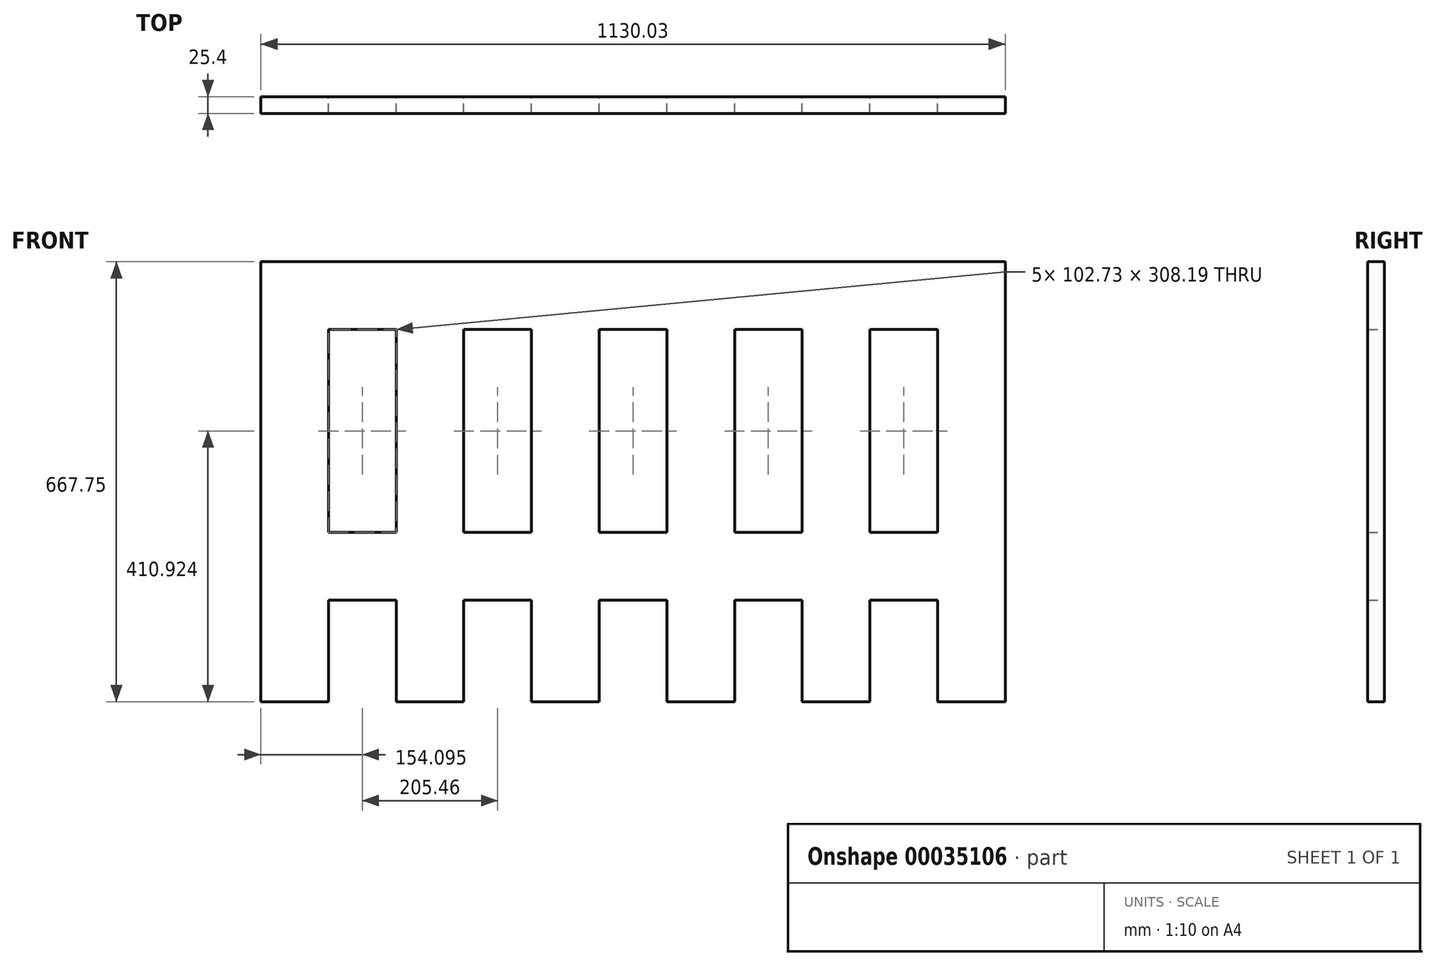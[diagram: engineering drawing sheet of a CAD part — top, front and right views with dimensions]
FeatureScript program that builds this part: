
annotation { "Feature Type Name" : "Feature", "Feature Type Description" : "" }
export const myFeature = defineFeature(function(context is Context, id is Id, definition is map)
    precondition{}
    {
        {
            var Q0;
            Q0=qCreatedBy(makeId("Front.planeOp"),FACE);
            var sketch = newSketch(context, id + "F0", { "sketchPlane" : qUnion([Q0])});
            skLineSegment(sketch, "E0", {"start": v(308.5, 268.75) * mm, "end": v(308.5, -399) * mm});
            skLineSegment(sketch, "E1", {"start": v(308.5, -399) * mm, "end": v(205.76, -399) * mm});
            skLineSegment(sketch, "E2", {"start": v(-821.54, -399) * mm, "end": v(-821.54, 268.75) * mm});
            skLineSegment(sketch, "E3", {"start": v(-821.54, 268.75) * mm, "end": v(308.5, 268.75) * mm});
            skLineSegment(sketch, "E4", {"start": v(-821.54, -244.9) * mm, "end": v(308.5, -244.9) * mm});
            skLineSegment(sketch, "E5", {"start": v(-821.54, -142.17) * mm, "end": v(308.5, -142.17) * mm});
            skLineSegment(sketch, "E6", {"start": v(-821.54, 166.02) * mm, "end": v(308.5, 166.02) * mm});
            skLineSegment(sketch, "E7", {"start": v(-718.81, 268.75) * mm, "end": v(-718.81, -399) * mm});
            skLineSegment(sketch, "E8", {"start": v(-616.08, 268.75) * mm, "end": v(-616.08, -399) * mm});
            skLineSegment(sketch, "E9", {"start": v(-513.35, 268.75) * mm, "end": v(-513.35, -399) * mm});
            skLineSegment(sketch, "E10", {"start": v(-410.62, 268.75) * mm, "end": v(-410.62, -399) * mm});
            skLineSegment(sketch, "E11", {"start": v(-307.89, 268.75) * mm, "end": v(-307.89, -399) * mm});
            skLineSegment(sketch, "E12", {"start": v(-205.16, 268.75) * mm, "end": v(-205.16, -399) * mm});
            skLineSegment(sketch, "E13", {"start": v(-102.43, 268.75) * mm, "end": v(-102.43, -399) * mm});
            skLineSegment(sketch, "E14", {"start": v(0.3, 268.75) * mm, "end": v(0.3, -399) * mm});
            skLineSegment(sketch, "E15", {"start": v(103.03, 268.75) * mm, "end": v(103.03, -399) * mm});
            skLineSegment(sketch, "E16", {"start": v(205.76, 268.75) * mm, "end": v(205.76, -399) * mm});
            skLineSegment(sketch, "E17.trimOffspring", {"start": v(-718.81, -399) * mm, "end": v(-821.54, -399) * mm});
            skLineSegment(sketch, "E18.trimOffspring", {"start": v(-513.35, -399) * mm, "end": v(-616.08, -399) * mm});
            skLineSegment(sketch, "E19.trimOffspring", {"start": v(-307.89, -399) * mm, "end": v(-410.62, -399) * mm});
            skLineSegment(sketch, "E20.trimOffspring", {"start": v(-102.43, -399) * mm, "end": v(-205.16, -399) * mm});
            skLineSegment(sketch, "E21.trimOffspring", {"start": v(103.03, -399) * mm, "end": v(0.3, -399) * mm});
            skLineSegment(sketch, "E22", {"start": v(-821.54, 268.75) * mm, "end": v(-821.54, 344.95) * mm});
            skLineSegment(sketch, "E23", {"start": v(308.5, 345.8) * mm, "end": v(308.5, 268.75) * mm});
            skLineSegment(sketch, "E24", {"start": v(-718.81, 268.75) * mm, "end": v(-718.87, 345.03) * mm});
            skLineSegment(sketch, "E25", {"start": v(-821.54, 344.95) * mm, "end": v(-770.18, 422.84) * mm});
            skLineSegment(sketch, "E26", {"start": v(-616.08, 268.75) * mm, "end": v(-616.14, 345.1) * mm});
            skLineSegment(sketch, "E27", {"start": v(-616.14, 345.1) * mm, "end": v(-564.72, 422.84) * mm});
            skLineSegment(sketch, "E28", {"start": v(-410.62, 268.75) * mm, "end": v(-410.68, 345.26) * mm});
            skLineSegment(sketch, "E29", {"start": v(-410.68, 345.26) * mm, "end": v(-359.25, 422.84) * mm});
            skLineSegment(sketch, "E30", {"start": v(-205.16, 268.75) * mm, "end": v(-205.16, 345.41) * mm});
            skLineSegment(sketch, "E31", {"start": v(-205.16, 345.41) * mm, "end": v(-153.8, 422.84) * mm});
            skLineSegment(sketch, "E32", {"start": v(0.3, 268.75) * mm, "end": v(0.3, 345.57) * mm});
            skLineSegment(sketch, "E33", {"start": v(0.3, 345.57) * mm, "end": v(51.67, 422.84) * mm});
            skLineSegment(sketch, "E34", {"start": v(205.76, 268.75) * mm, "end": v(205.76, 345.72) * mm});
            skLineSegment(sketch, "E35", {"start": v(205.76, 345.72) * mm, "end": v(257.13, 422.84) * mm});
            skLineSegment(sketch, "E36", {"start": v(-770.18, 422.84) * mm, "end": v(-718.87, 345.03) * mm});
            skLineSegment(sketch, "E37", {"start": v(-513.35, 268.75) * mm, "end": v(-513.35, 345.18) * mm});
            skLineSegment(sketch, "E38", {"start": v(-513.35, 345.18) * mm, "end": v(-564.72, 422.84) * mm});
            skLineSegment(sketch, "E39", {"start": v(-307.89, 268.75) * mm, "end": v(-307.89, 345.33) * mm});
            skLineSegment(sketch, "E40", {"start": v(-307.89, 345.33) * mm, "end": v(-359.25, 422.84) * mm});
            skLineSegment(sketch, "E41", {"start": v(-102.43, 268.75) * mm, "end": v(-102.43, 345.49) * mm});
            skLineSegment(sketch, "E42", {"start": v(-102.43, 345.49) * mm, "end": v(-153.8, 422.84) * mm});
            skLineSegment(sketch, "E43", {"start": v(103.03, 268.75) * mm, "end": v(103.03, 345.64) * mm});
            skLineSegment(sketch, "E44", {"start": v(103.03, 345.64) * mm, "end": v(51.67, 422.84) * mm});
            skLineSegment(sketch, "E45", {"start": v(257.13, 422.84) * mm, "end": v(308.5, 345.8) * mm});
            skSolve(sketch);
        }
        {
            var Q0;
            {var subQ1=sQuery(id+"F0.wireOp",EDGE,"c169b1e0-b60f-4d37-8ace-ff5277b2fe1d");Q0=makeQuery(id+"F0.imprint","IMPRINT",FACE,{"disambiguationData":[TD([[makeQuery(id+"F0.imprint","IMPRINT",EDGE,{"derivedFrom":subQ1}),-1.0]])]});}
            var Q1;
            {var subQ1=sQuery(id+"F0.wireOp",EDGE,"E6");var subQ5=sQuery(id+"F0.wireOp",EDGE,"E2");var subQ6=makeQuery(id+"F0.imprint","INTERSECT",VERTEX,{"derivedFrom":[subQ5,subQ1]});Q1=makeQuery(id+"F0.imprint","IMPRINT",FACE,{"disambiguationData":[TD([[makeQuery(id+"F0.imprint","IMPRINT",EDGE,{"disambiguationData":[TD([[subQ6,-1.0]])],"derivedFrom":subQ1}),1.0]])]});}
            var Q2;
            {var subQ3=sQuery(id+"F0.wireOp",EDGE,"E5");var subQ5=sQuery(id+"F0.wireOp",EDGE,"E2");var subQ7=makeQuery(id+"F0.imprint","INTERSECT",VERTEX,{"derivedFrom":[subQ5,subQ3]});Q2=makeQuery(id+"F0.imprint","IMPRINT",FACE,{"disambiguationData":[TD([[makeQuery(id+"F0.imprint","IMPRINT",EDGE,{"disambiguationData":[TD([[subQ7,-1.0]])],"derivedFrom":subQ5}),-1.0]])]});}
            var Q3;
            {var subQ3=sQuery(id+"F0.wireOp",EDGE,"E4");var subQ5=sQuery(id+"F0.wireOp",EDGE,"E2");var subQ7=makeQuery(id+"F0.imprint","INTERSECT",VERTEX,{"derivedFrom":[subQ5,subQ3]});Q3=makeQuery(id+"F0.imprint","IMPRINT",FACE,{"disambiguationData":[TD([[makeQuery(id+"F0.imprint","IMPRINT",EDGE,{"disambiguationData":[TD([[subQ7,-1.0]])],"derivedFrom":subQ5}),-1.0]])]});}
            var Q4;
            {var subQ0=sQuery(id+"F0.wireOp",EDGE,"E17.trimOffspring");Q4=makeQuery(id+"F0.imprint","IMPRINT",FACE,{"disambiguationData":[TD([[makeQuery(id+"F0.imprint","IMPRINT",EDGE,{"derivedFrom":subQ0}),-1.0]])]});}
            var Q5;
            {var subQ0=sQuery(id+"F0.wireOp",EDGE,"E8");var subQ3=sQuery(id+"F0.wireOp",EDGE,"E4");var subQ4=makeQuery(id+"F0.imprint","INTERSECT",VERTEX,{"derivedFrom":[subQ3,subQ0]});Q5=makeQuery(id+"F0.imprint","IMPRINT",FACE,{"disambiguationData":[TD([[makeQuery(id+"F0.imprint","IMPRINT",EDGE,{"disambiguationData":[TD([[subQ4,-1.0]])],"derivedFrom":subQ3}),1.0]])]});}
            var Q6;
            {var subQ3=sQuery(id+"F0.wireOp",EDGE,"E5");var subQ5=sQuery(id+"F0.wireOp",EDGE,"E8");var subQ7=makeQuery(id+"F0.imprint","INTERSECT",VERTEX,{"derivedFrom":[subQ3,subQ5]});Q6=makeQuery(id+"F0.imprint","IMPRINT",FACE,{"disambiguationData":[TD([[makeQuery(id+"F0.imprint","IMPRINT",EDGE,{"disambiguationData":[TD([[subQ7,-1.0]])],"derivedFrom":subQ3}),1.0]])]});}
            var Q7;
            {var subQ1=sQuery(id+"F0.wireOp",EDGE,"E6");var subQ5=sQuery(id+"F0.wireOp",EDGE,"E8");var subQ6=makeQuery(id+"F0.imprint","INTERSECT",VERTEX,{"derivedFrom":[subQ1,subQ5]});Q7=makeQuery(id+"F0.imprint","IMPRINT",FACE,{"disambiguationData":[TD([[makeQuery(id+"F0.imprint","IMPRINT",EDGE,{"disambiguationData":[TD([[subQ6,-1.0]])],"derivedFrom":subQ1}),1.0]])]});}
            var Q8;
            {var subQ1=sQuery(id+"F0.wireOp",EDGE,"92349909-26e1-4acf-9d0d-d4a8c5e57fef");Q8=makeQuery(id+"F0.imprint","IMPRINT",FACE,{"disambiguationData":[TD([[makeQuery(id+"F0.imprint","IMPRINT",EDGE,{"derivedFrom":subQ1}),-1.0]])]});}
            var Q9;
            {var subQ1=sQuery(id+"F0.wireOp",EDGE,"cf5320f6-0652-4101-89c0-8b02578a7313");Q9=makeQuery(id+"F0.imprint","IMPRINT",FACE,{"disambiguationData":[TD([[makeQuery(id+"F0.imprint","IMPRINT",EDGE,{"derivedFrom":subQ1}),1.0]])]});}
            var Q10;
            {var subQ1=sQuery(id+"F0.wireOp",EDGE,"E6");var subQ5=sQuery(id+"F0.wireOp",EDGE,"E10");var subQ6=makeQuery(id+"F0.imprint","INTERSECT",VERTEX,{"derivedFrom":[subQ1,subQ5]});Q10=makeQuery(id+"F0.imprint","IMPRINT",FACE,{"disambiguationData":[TD([[makeQuery(id+"F0.imprint","IMPRINT",EDGE,{"disambiguationData":[TD([[subQ6,-1.0]])],"derivedFrom":subQ1}),1.0]])]});}
            var Q11;
            {var subQ3=sQuery(id+"F0.wireOp",EDGE,"E5");var subQ5=sQuery(id+"F0.wireOp",EDGE,"E10");var subQ7=makeQuery(id+"F0.imprint","INTERSECT",VERTEX,{"derivedFrom":[subQ3,subQ5]});Q11=makeQuery(id+"F0.imprint","IMPRINT",FACE,{"disambiguationData":[TD([[makeQuery(id+"F0.imprint","IMPRINT",EDGE,{"disambiguationData":[TD([[subQ7,-1.0]])],"derivedFrom":subQ3}),1.0]])]});}
            var Q12;
            {var subQ0=sQuery(id+"F0.wireOp",EDGE,"E19.trimOffspring");Q12=makeQuery(id+"F0.imprint","IMPRINT",FACE,{"disambiguationData":[TD([[makeQuery(id+"F0.imprint","IMPRINT",EDGE,{"derivedFrom":subQ0}),-1.0]])]});}
            var Q13;
            {var subQ0=sQuery(id+"F0.wireOp",EDGE,"E18.trimOffspring");Q13=makeQuery(id+"F0.imprint","IMPRINT",FACE,{"disambiguationData":[TD([[makeQuery(id+"F0.imprint","IMPRINT",EDGE,{"derivedFrom":subQ0}),-1.0]])]});}
            var Q14;
            {var subQ3=sQuery(id+"F0.wireOp",EDGE,"E4");var subQ5=sQuery(id+"F0.wireOp",EDGE,"E10");var subQ7=makeQuery(id+"F0.imprint","INTERSECT",VERTEX,{"derivedFrom":[subQ3,subQ5]});Q14=makeQuery(id+"F0.imprint","IMPRINT",FACE,{"disambiguationData":[TD([[makeQuery(id+"F0.imprint","IMPRINT",EDGE,{"disambiguationData":[TD([[subQ7,-1.0]])],"derivedFrom":subQ3}),1.0]])]});}
            var Q15;
            {var subQ3=sQuery(id+"F0.wireOp",EDGE,"E4");var subQ5=sQuery(id+"F0.wireOp",EDGE,"E12");var subQ7=makeQuery(id+"F0.imprint","INTERSECT",VERTEX,{"derivedFrom":[subQ3,subQ5]});Q15=makeQuery(id+"F0.imprint","IMPRINT",FACE,{"disambiguationData":[TD([[makeQuery(id+"F0.imprint","IMPRINT",EDGE,{"disambiguationData":[TD([[subQ7,-1.0]])],"derivedFrom":subQ3}),1.0]])]});}
            var Q16;
            {var subQ1=sQuery(id+"F0.wireOp",EDGE,"E6");var subQ5=sQuery(id+"F0.wireOp",EDGE,"E12");var subQ6=makeQuery(id+"F0.imprint","INTERSECT",VERTEX,{"derivedFrom":[subQ1,subQ5]});Q16=makeQuery(id+"F0.imprint","IMPRINT",FACE,{"disambiguationData":[TD([[makeQuery(id+"F0.imprint","IMPRINT",EDGE,{"disambiguationData":[TD([[subQ6,-1.0]])],"derivedFrom":subQ1}),1.0]])]});}
            var Q17;
            {var subQ0=sQuery(id+"F0.wireOp",EDGE,"E20.trimOffspring");Q17=makeQuery(id+"F0.imprint","IMPRINT",FACE,{"disambiguationData":[TD([[makeQuery(id+"F0.imprint","IMPRINT",EDGE,{"derivedFrom":subQ0}),-1.0]])]});}
            var Q18;
            {var subQ0=sQuery(id+"F0.wireOp",EDGE,"E21.trimOffspring");Q18=makeQuery(id+"F0.imprint","IMPRINT",FACE,{"disambiguationData":[TD([[makeQuery(id+"F0.imprint","IMPRINT",EDGE,{"derivedFrom":subQ0}),-1.0]])]});}
            var Q19;
            {var subQ3=sQuery(id+"F0.wireOp",EDGE,"E4");var subQ5=sQuery(id+"F0.wireOp",EDGE,"E14");var subQ7=makeQuery(id+"F0.imprint","INTERSECT",VERTEX,{"derivedFrom":[subQ3,subQ5]});Q19=makeQuery(id+"F0.imprint","IMPRINT",FACE,{"disambiguationData":[TD([[makeQuery(id+"F0.imprint","IMPRINT",EDGE,{"disambiguationData":[TD([[subQ7,-1.0]])],"derivedFrom":subQ3}),1.0]])]});}
            var Q20;
            {var subQ3=sQuery(id+"F0.wireOp",EDGE,"E5");var subQ5=sQuery(id+"F0.wireOp",EDGE,"E14");var subQ7=makeQuery(id+"F0.imprint","INTERSECT",VERTEX,{"derivedFrom":[subQ3,subQ5]});Q20=makeQuery(id+"F0.imprint","IMPRINT",FACE,{"disambiguationData":[TD([[makeQuery(id+"F0.imprint","IMPRINT",EDGE,{"disambiguationData":[TD([[subQ7,-1.0]])],"derivedFrom":subQ3}),1.0]])]});}
            var Q21;
            {var subQ0=sQuery(id+"F0.wireOp",EDGE,"E12");var subQ3=sQuery(id+"F0.wireOp",EDGE,"E5");var subQ4=makeQuery(id+"F0.imprint","INTERSECT",VERTEX,{"derivedFrom":[subQ3,subQ0]});Q21=makeQuery(id+"F0.imprint","IMPRINT",FACE,{"disambiguationData":[TD([[makeQuery(id+"F0.imprint","IMPRINT",EDGE,{"disambiguationData":[TD([[subQ4,-1.0]])],"derivedFrom":subQ3}),1.0]])]});}
            var Q22;
            {var subQ1=sQuery(id+"F0.wireOp",EDGE,"cce5696a-d977-45ba-8bba-f19669daab51");Q22=makeQuery(id+"F0.imprint","IMPRINT",FACE,{"disambiguationData":[TD([[makeQuery(id+"F0.imprint","IMPRINT",EDGE,{"derivedFrom":subQ1}),-1.0]])]});}
            var Q23;
            {var subQ1=sQuery(id+"F0.wireOp",EDGE,"E6");var subQ5=sQuery(id+"F0.wireOp",EDGE,"E14");var subQ6=makeQuery(id+"F0.imprint","INTERSECT",VERTEX,{"derivedFrom":[subQ1,subQ5]});Q23=makeQuery(id+"F0.imprint","IMPRINT",FACE,{"disambiguationData":[TD([[makeQuery(id+"F0.imprint","IMPRINT",EDGE,{"disambiguationData":[TD([[subQ6,-1.0]])],"derivedFrom":subQ1}),1.0]])]});}
            var Q24;
            {var subQ1=sQuery(id+"F0.wireOp",EDGE,"c1ef5110-5076-4814-bbc6-836c40303233");Q24=makeQuery(id+"F0.imprint","IMPRINT",FACE,{"disambiguationData":[TD([[makeQuery(id+"F0.imprint","IMPRINT",EDGE,{"derivedFrom":subQ1}),-1.0]])]});}
            var Q25;
            {var subQ1=sQuery(id+"F0.wireOp",EDGE,"9a15e80a-7592-4d47-aeb3-d8fba71619d8");Q25=makeQuery(id+"F0.imprint","IMPRINT",FACE,{"disambiguationData":[TD([[makeQuery(id+"F0.imprint","IMPRINT",EDGE,{"derivedFrom":subQ1}),-1.0]])]});}
            var Q26;
            {var subQ1=sQuery(id+"F0.wireOp",EDGE,"E6");var subQ5=sQuery(id+"F0.wireOp",EDGE,"E0");var subQ6=makeQuery(id+"F0.imprint","INTERSECT",VERTEX,{"derivedFrom":[subQ5,subQ1]});Q26=makeQuery(id+"F0.imprint","IMPRINT",FACE,{"disambiguationData":[TD([[makeQuery(id+"F0.imprint","IMPRINT",EDGE,{"disambiguationData":[TD([[subQ6,1.0]])],"derivedFrom":subQ1}),1.0]])]});}
            var Q27;
            {var subQ3=sQuery(id+"F0.wireOp",EDGE,"E5");var subQ5=sQuery(id+"F0.wireOp",EDGE,"E0");var subQ7=makeQuery(id+"F0.imprint","INTERSECT",VERTEX,{"derivedFrom":[subQ5,subQ3]});Q27=makeQuery(id+"F0.imprint","IMPRINT",FACE,{"disambiguationData":[TD([[makeQuery(id+"F0.imprint","IMPRINT",EDGE,{"disambiguationData":[TD([[subQ7,1.0]])],"derivedFrom":subQ5}),-1.0]])]});}
            var Q28;
            {var subQ3=sQuery(id+"F0.wireOp",EDGE,"E4");var subQ5=sQuery(id+"F0.wireOp",EDGE,"E0");var subQ7=makeQuery(id+"F0.imprint","INTERSECT",VERTEX,{"derivedFrom":[subQ5,subQ3]});Q28=makeQuery(id+"F0.imprint","IMPRINT",FACE,{"disambiguationData":[TD([[makeQuery(id+"F0.imprint","IMPRINT",EDGE,{"disambiguationData":[TD([[subQ7,1.0]])],"derivedFrom":subQ5}),-1.0]])]});}
            var Q29;
            {var subQ3=sQuery(id+"F0.wireOp",EDGE,"E1");Q29=makeQuery(id+"F0.imprint","IMPRINT",FACE,{"disambiguationData":[TD([[makeQuery(id+"F0.imprint","IMPRINT",EDGE,{"derivedFrom":subQ3}),-1.0]])]});}
            var Q30;
            {var subQ1=sQuery(id+"F0.wireOp",EDGE,"E6");var subQ5=sQuery(id+"F0.wireOp",EDGE,"E7");var subQ6=makeQuery(id+"F0.imprint","INTERSECT",VERTEX,{"derivedFrom":[subQ1,subQ5]});Q30=makeQuery(id+"F0.imprint","IMPRINT",FACE,{"disambiguationData":[TD([[makeQuery(id+"F0.imprint","IMPRINT",EDGE,{"disambiguationData":[TD([[subQ6,-1.0]])],"derivedFrom":subQ1}),1.0]])]});}
            var Q31;
            {var subQ3=sQuery(id+"F0.wireOp",EDGE,"E4");var subQ5=sQuery(id+"F0.wireOp",EDGE,"E7");var subQ7=makeQuery(id+"F0.imprint","INTERSECT",VERTEX,{"derivedFrom":[subQ3,subQ5]});Q31=makeQuery(id+"F0.imprint","IMPRINT",FACE,{"disambiguationData":[TD([[makeQuery(id+"F0.imprint","IMPRINT",EDGE,{"disambiguationData":[TD([[subQ7,-1.0]])],"derivedFrom":subQ3}),1.0]])]});}
            var Q32;
            {var subQ3=sQuery(id+"F0.wireOp",EDGE,"E4");var subQ5=sQuery(id+"F0.wireOp",EDGE,"E9");var subQ7=makeQuery(id+"F0.imprint","INTERSECT",VERTEX,{"derivedFrom":[subQ3,subQ5]});Q32=makeQuery(id+"F0.imprint","IMPRINT",FACE,{"disambiguationData":[TD([[makeQuery(id+"F0.imprint","IMPRINT",EDGE,{"disambiguationData":[TD([[subQ7,-1.0]])],"derivedFrom":subQ3}),1.0]])]});}
            var Q33;
            {var subQ1=sQuery(id+"F0.wireOp",EDGE,"E6");var subQ5=sQuery(id+"F0.wireOp",EDGE,"E9");var subQ6=makeQuery(id+"F0.imprint","INTERSECT",VERTEX,{"derivedFrom":[subQ1,subQ5]});Q33=makeQuery(id+"F0.imprint","IMPRINT",FACE,{"disambiguationData":[TD([[makeQuery(id+"F0.imprint","IMPRINT",EDGE,{"disambiguationData":[TD([[subQ6,-1.0]])],"derivedFrom":subQ1}),1.0]])]});}
            var Q34;
            {var subQ0=sQuery(id+"F0.wireOp",EDGE,"E11");var subQ1=sQuery(id+"F0.wireOp",EDGE,"E6");var subQ2=makeQuery(id+"F0.imprint","INTERSECT",VERTEX,{"derivedFrom":[subQ1,subQ0]});Q34=makeQuery(id+"F0.imprint","IMPRINT",FACE,{"disambiguationData":[TD([[makeQuery(id+"F0.imprint","IMPRINT",EDGE,{"disambiguationData":[TD([[subQ2,-1.0]])],"derivedFrom":subQ1}),1.0]])]});}
            var Q35;
            {var subQ3=sQuery(id+"F0.wireOp",EDGE,"E4");var subQ5=sQuery(id+"F0.wireOp",EDGE,"E11");var subQ7=makeQuery(id+"F0.imprint","INTERSECT",VERTEX,{"derivedFrom":[subQ3,subQ5]});Q35=makeQuery(id+"F0.imprint","IMPRINT",FACE,{"disambiguationData":[TD([[makeQuery(id+"F0.imprint","IMPRINT",EDGE,{"disambiguationData":[TD([[subQ7,-1.0]])],"derivedFrom":subQ3}),1.0]])]});}
            var Q36;
            {var subQ3=sQuery(id+"F0.wireOp",EDGE,"E4");var subQ5=sQuery(id+"F0.wireOp",EDGE,"E13");var subQ7=makeQuery(id+"F0.imprint","INTERSECT",VERTEX,{"derivedFrom":[subQ3,subQ5]});Q36=makeQuery(id+"F0.imprint","IMPRINT",FACE,{"disambiguationData":[TD([[makeQuery(id+"F0.imprint","IMPRINT",EDGE,{"disambiguationData":[TD([[subQ7,-1.0]])],"derivedFrom":subQ3}),1.0]])]});}
            var Q37;
            {var subQ1=sQuery(id+"F0.wireOp",EDGE,"E6");var subQ5=sQuery(id+"F0.wireOp",EDGE,"E13");var subQ6=makeQuery(id+"F0.imprint","INTERSECT",VERTEX,{"derivedFrom":[subQ1,subQ5]});Q37=makeQuery(id+"F0.imprint","IMPRINT",FACE,{"disambiguationData":[TD([[makeQuery(id+"F0.imprint","IMPRINT",EDGE,{"disambiguationData":[TD([[subQ6,-1.0]])],"derivedFrom":subQ1}),1.0]])]});}
            var Q38;
            {var subQ1=sQuery(id+"F0.wireOp",EDGE,"E6");var subQ5=sQuery(id+"F0.wireOp",EDGE,"E15");var subQ6=makeQuery(id+"F0.imprint","INTERSECT",VERTEX,{"derivedFrom":[subQ1,subQ5]});Q38=makeQuery(id+"F0.imprint","IMPRINT",FACE,{"disambiguationData":[TD([[makeQuery(id+"F0.imprint","IMPRINT",EDGE,{"disambiguationData":[TD([[subQ6,-1.0]])],"derivedFrom":subQ1}),1.0]])]});}
            var Q39;
            {var subQ3=sQuery(id+"F0.wireOp",EDGE,"E4");var subQ5=sQuery(id+"F0.wireOp",EDGE,"E15");var subQ7=makeQuery(id+"F0.imprint","INTERSECT",VERTEX,{"derivedFrom":[subQ3,subQ5]});Q39=makeQuery(id+"F0.imprint","IMPRINT",FACE,{"disambiguationData":[TD([[makeQuery(id+"F0.imprint","IMPRINT",EDGE,{"disambiguationData":[TD([[subQ7,-1.0]])],"derivedFrom":subQ3}),1.0]])]});}
            extrude(context, id + "F1", {"entities" : qUnion([Q0, Q1, Q2, Q3, Q4, Q5, Q6, Q7, Q8, Q9, Q10, Q11, Q12, Q13, Q14, Q15, Q16, Q17, Q18, Q19, Q20, Q21, Q22, Q23, Q24, Q25, Q26, Q27, Q28, Q29, Q30, Q31, Q32, Q33, Q34, Q35, Q36, Q37, Q38, Q39]), "depth" : 25.4 * mm});
        }
    });
